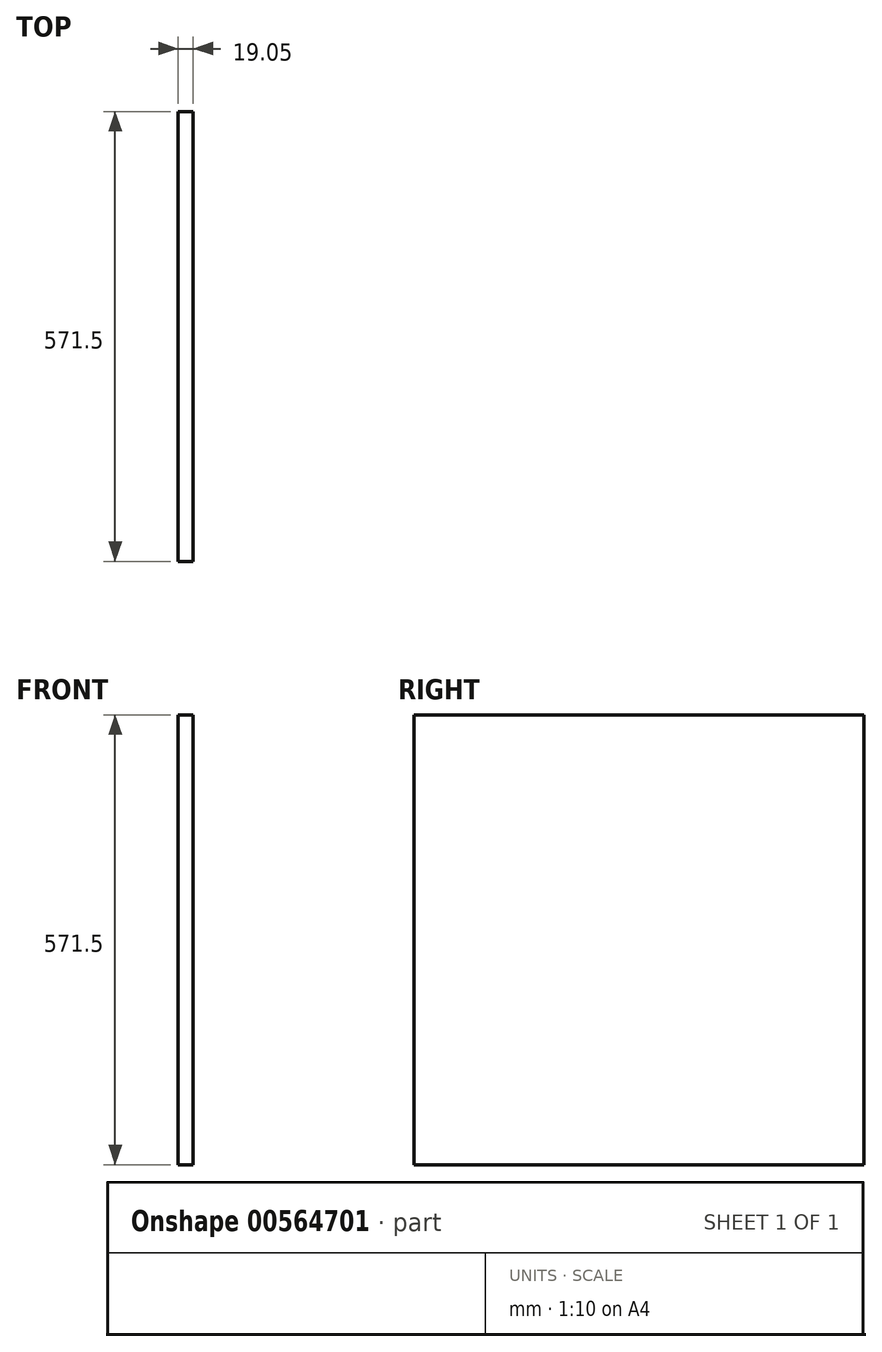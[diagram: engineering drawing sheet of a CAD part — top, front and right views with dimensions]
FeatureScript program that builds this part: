
annotation { "Feature Type Name" : "Feature", "Feature Type Description" : "" }
export const myFeature = defineFeature(function(context is Context, id is Id, definition is map)
    precondition{}
    {
        {
            var Q0;
            Q0=qCreatedBy(makeId("Right.planeOp"),FACE);
            var sketch = newSketch(context, id + "F0", { "sketchPlane" : qUnion([Q0])});
            skLineSegment(sketch, "E0.bottom", {"start": v(285.75, 285.75) * mm, "end": v(-285.75, 285.75) * mm});
            skLineSegment(sketch, "E0.top", {"start": v(285.75, -285.75) * mm, "end": v(-285.75, -285.75) * mm});
            skLineSegment(sketch, "E0.left", {"start": v(285.75, 285.75) * mm, "end": v(285.75, -285.75) * mm});
            skLineSegment(sketch, "E0.right", {"start": v(-285.75, 285.75) * mm, "end": v(-285.75, -285.75) * mm});
            skPoint(sketch, "E0.middle", {"position": v(0, 0) * mm});
            skSolve(sketch);
        }
        {
            var Q0;
            Q0=qSketchRegion(id+"F0",true);
            extrude(context, id + "F1", {"entities" : qUnion([Q0]), "depth" : 19.05 * mm, "offsetDistance" : 25.4 * mm});
        }
    });
